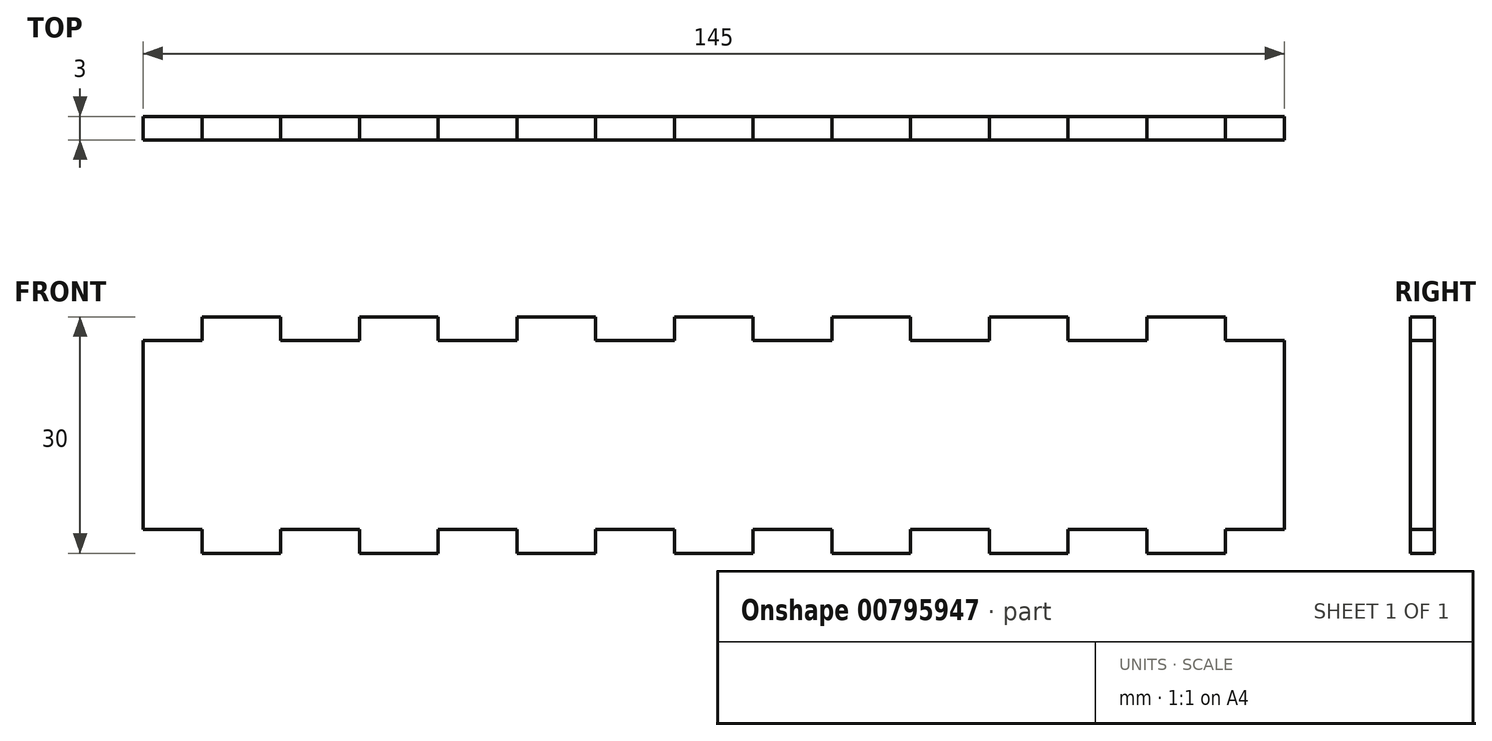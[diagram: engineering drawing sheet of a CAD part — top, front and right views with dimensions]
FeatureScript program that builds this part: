
annotation { "Feature Type Name" : "Feature", "Feature Type Description" : "" }
export const myFeature = defineFeature(function(context is Context, id is Id, definition is map)
    precondition{}
    {
        {
            var Q0;
            Q0=qCreatedBy(makeId("Front.planeOp"),FACE);
            var sketch = newSketch(context, id + "F0", { "sketchPlane" : qUnion([Q0])});
            skLineSegment(sketch, "E0.bottom", {"start": v(72.5, 15) * mm, "end": v(-72.5, 15) * mm});
            skLineSegment(sketch, "E0.top", {"start": v(72.5, -15) * mm, "end": v(-72.5, -15) * mm});
            skLineSegment(sketch, "E0.left", {"start": v(72.5, 15) * mm, "end": v(72.5, -15) * mm});
            skLineSegment(sketch, "E0.right", {"start": v(-72.5, 15) * mm, "end": v(-72.5, -15) * mm});
            skPoint(sketch, "E0.middle", {"position": v(0, 0) * mm});
            skSolve(sketch);
        }
        {
            var Q0;
            Q0=makeQuery(id+"F0.imprint","IMPRINT",FACE,{"disambiguationData":[TD([[makeQuery(id+"F0.imprint","IMPRINT",EDGE,{"derivedFrom":sQuery(id+"F0.wireOp",EDGE,"E0.bottom")}),1.0]])]});
            extrude(context, id + "F1", {"entities" : qUnion([Q0]), "depth" : 3 * mm, "offsetDistance" : 25 * mm});
        }
        {
            var Q0;
            Q0=makeQuery(id+"F1.opExtrude","CAP_FACE",FACE,{"disambiguationData":[OSD([sQuery(id+"F0.wireOp",EDGE,"E0.bottom"),sQuery(id+"F0.wireOp",EDGE,"E0.top"),sQuery(id+"F0.wireOp",EDGE,"E0.left"),sQuery(id+"F0.wireOp",EDGE,"E0.right")])],"isStart":false});
            var sketch = newSketch(context, id + "F2", { "sketchPlane" : qUnion([Q0])});
            skLineSegment(sketch, "E1", {"start": v(-75, -15) * mm, "end": v(-72.5, -15) * mm, "construction": true});
            skLineSegment(sketch, "E2.bottom", {"start": v(-75, -15) * mm, "end": v(-65, -15) * mm});
            skLineSegment(sketch, "E2.top", {"start": v(-75, -12) * mm, "end": v(-65, -12) * mm});
            skLineSegment(sketch, "E2.left", {"start": v(-75, -15) * mm, "end": v(-75, -12) * mm});
            skLineSegment(sketch, "E2.right", {"start": v(-65, -15) * mm, "end": v(-65, -12) * mm});
            skLineSegment(sketch, "E3.0.1.0", {"start": v(-75, 15) * mm, "end": v(-65, 15) * mm});
            skLineSegment(sketch, "E3.0.1.1", {"start": v(-75, 12) * mm, "end": v(-65, 12) * mm});
            skLineSegment(sketch, "E3.0.1.2", {"start": v(-65, 12) * mm, "end": v(-65, 15) * mm});
            skLineSegment(sketch, "E3.0.1.3", {"start": v(-75, 12) * mm, "end": v(-75, 15) * mm});
            skLineSegment(sketch, "E3.1.0.0", {"start": v(-55, -12) * mm, "end": v(-45, -12) * mm});
            skLineSegment(sketch, "E3.1.0.1", {"start": v(-55, -15) * mm, "end": v(-45, -15) * mm});
            skLineSegment(sketch, "E3.1.0.2", {"start": v(-45, -15) * mm, "end": v(-45, -12) * mm});
            skLineSegment(sketch, "E3.1.0.3", {"start": v(-55, -15) * mm, "end": v(-55, -12) * mm});
            skLineSegment(sketch, "E3.1.1.0", {"start": v(-55, 15) * mm, "end": v(-45, 15) * mm});
            skLineSegment(sketch, "E3.1.1.1", {"start": v(-55, 12) * mm, "end": v(-45, 12) * mm});
            skLineSegment(sketch, "E3.1.1.2", {"start": v(-45, 12) * mm, "end": v(-45, 15) * mm});
            skLineSegment(sketch, "E3.1.1.3", {"start": v(-55, 12) * mm, "end": v(-55, 15) * mm});
            skLineSegment(sketch, "E3.2.0.0", {"start": v(-35, -12) * mm, "end": v(-25, -12) * mm});
            skLineSegment(sketch, "E3.2.0.1", {"start": v(-35, -15) * mm, "end": v(-25, -15) * mm});
            skLineSegment(sketch, "E3.2.0.2", {"start": v(-25, -15) * mm, "end": v(-25, -12) * mm});
            skLineSegment(sketch, "E3.2.0.3", {"start": v(-35, -15) * mm, "end": v(-35, -12) * mm});
            skLineSegment(sketch, "E3.2.1.0", {"start": v(-35, 15) * mm, "end": v(-25, 15) * mm});
            skLineSegment(sketch, "E3.2.1.1", {"start": v(-35, 12) * mm, "end": v(-25, 12) * mm});
            skLineSegment(sketch, "E3.2.1.2", {"start": v(-25, 12) * mm, "end": v(-25, 15) * mm});
            skLineSegment(sketch, "E3.2.1.3", {"start": v(-35, 12) * mm, "end": v(-35, 15) * mm});
            skLineSegment(sketch, "E3.3.0.0", {"start": v(-15, -12) * mm, "end": v(-5, -12) * mm});
            skLineSegment(sketch, "E3.3.0.1", {"start": v(-15, -15) * mm, "end": v(-5, -15) * mm});
            skLineSegment(sketch, "E3.3.0.2", {"start": v(-5, -15) * mm, "end": v(-5, -12) * mm});
            skLineSegment(sketch, "E3.3.0.3", {"start": v(-15, -15) * mm, "end": v(-15, -12) * mm});
            skLineSegment(sketch, "E3.3.1.0", {"start": v(-15, 15) * mm, "end": v(-5, 15) * mm});
            skLineSegment(sketch, "E3.3.1.1", {"start": v(-15, 12) * mm, "end": v(-5, 12) * mm});
            skLineSegment(sketch, "E3.3.1.2", {"start": v(-5, 12) * mm, "end": v(-5, 15) * mm});
            skLineSegment(sketch, "E3.3.1.3", {"start": v(-15, 12) * mm, "end": v(-15, 15) * mm});
            skLineSegment(sketch, "E3.4.0.0", {"start": v(5, -12) * mm, "end": v(15, -12) * mm});
            skLineSegment(sketch, "E3.4.0.1", {"start": v(5, -15) * mm, "end": v(15, -15) * mm});
            skLineSegment(sketch, "E3.4.0.2", {"start": v(15, -15) * mm, "end": v(15, -12) * mm});
            skLineSegment(sketch, "E3.4.0.3", {"start": v(5, -15) * mm, "end": v(5, -12) * mm});
            skLineSegment(sketch, "E3.4.1.0", {"start": v(5, 15) * mm, "end": v(15, 15) * mm});
            skLineSegment(sketch, "E3.4.1.1", {"start": v(5, 12) * mm, "end": v(15, 12) * mm});
            skLineSegment(sketch, "E3.4.1.2", {"start": v(15, 12) * mm, "end": v(15, 15) * mm});
            skLineSegment(sketch, "E3.4.1.3", {"start": v(5, 12) * mm, "end": v(5, 15) * mm});
            skLineSegment(sketch, "E3.5.0.0", {"start": v(25, -12) * mm, "end": v(35, -12) * mm});
            skLineSegment(sketch, "E3.5.0.1", {"start": v(25, -15) * mm, "end": v(35, -15) * mm});
            skLineSegment(sketch, "E3.5.0.2", {"start": v(35, -15) * mm, "end": v(35, -12) * mm});
            skLineSegment(sketch, "E3.5.0.3", {"start": v(25, -15) * mm, "end": v(25, -12) * mm});
            skLineSegment(sketch, "E3.5.1.0", {"start": v(25, 15) * mm, "end": v(35, 15) * mm});
            skLineSegment(sketch, "E3.5.1.1", {"start": v(25, 12) * mm, "end": v(35, 12) * mm});
            skLineSegment(sketch, "E3.5.1.2", {"start": v(35, 12) * mm, "end": v(35, 15) * mm});
            skLineSegment(sketch, "E3.5.1.3", {"start": v(25, 12) * mm, "end": v(25, 15) * mm});
            skLineSegment(sketch, "E3.6.0.0", {"start": v(45, -12) * mm, "end": v(55, -12) * mm});
            skLineSegment(sketch, "E3.6.0.1", {"start": v(45, -15) * mm, "end": v(55, -15) * mm});
            skLineSegment(sketch, "E3.6.0.2", {"start": v(55, -15) * mm, "end": v(55, -12) * mm});
            skLineSegment(sketch, "E3.6.0.3", {"start": v(45, -15) * mm, "end": v(45, -12) * mm});
            skLineSegment(sketch, "E3.6.1.0", {"start": v(45, 15) * mm, "end": v(55, 15) * mm});
            skLineSegment(sketch, "E3.6.1.1", {"start": v(45, 12) * mm, "end": v(55, 12) * mm});
            skLineSegment(sketch, "E3.6.1.2", {"start": v(55, 12) * mm, "end": v(55, 15) * mm});
            skLineSegment(sketch, "E3.6.1.3", {"start": v(45, 12) * mm, "end": v(45, 15) * mm});
            skLineSegment(sketch, "E3.direction1", {"start": v(-75, -12) * mm, "end": v(-55, -12) * mm, "construction": true});
            skLineSegment(sketch, "E3.direction2", {"start": v(-75, -12) * mm, "end": v(-75, 15) * mm, "construction": true});
            skLineSegment(sketch, "E4.0.7.0", {"start": v(65, -12) * mm, "end": v(75, -12) * mm});
            skLineSegment(sketch, "E4.3.7.0", {"start": v(65, -15) * mm, "end": v(75, -15) * mm});
            skLineSegment(sketch, "E4.6.7.0", {"start": v(75, -15) * mm, "end": v(75, -12) * mm});
            skLineSegment(sketch, "E4.9.7.0", {"start": v(65, -15) * mm, "end": v(65, -12) * mm});
            skLineSegment(sketch, "E4.0.7.1", {"start": v(65, 15) * mm, "end": v(75, 15) * mm});
            skLineSegment(sketch, "E4.3.7.1", {"start": v(65, 12) * mm, "end": v(75, 12) * mm});
            skLineSegment(sketch, "E4.6.7.1", {"start": v(75, 12) * mm, "end": v(75, 15) * mm});
            skLineSegment(sketch, "E4.9.7.1", {"start": v(65, 12) * mm, "end": v(65, 15) * mm});
            skSolve(sketch);
        }
        {
            var Q0;
            Q0=qSketchRegion(id+"F2",true);
            extrude(context, id + "F3", {"entities" : qUnion([Q0]), "operationType" : NewBodyOperationType.REMOVE, "oppositeDirection" : true, "depth" : 25 * mm, "offsetDistance" : 25 * mm});
        }
    });
